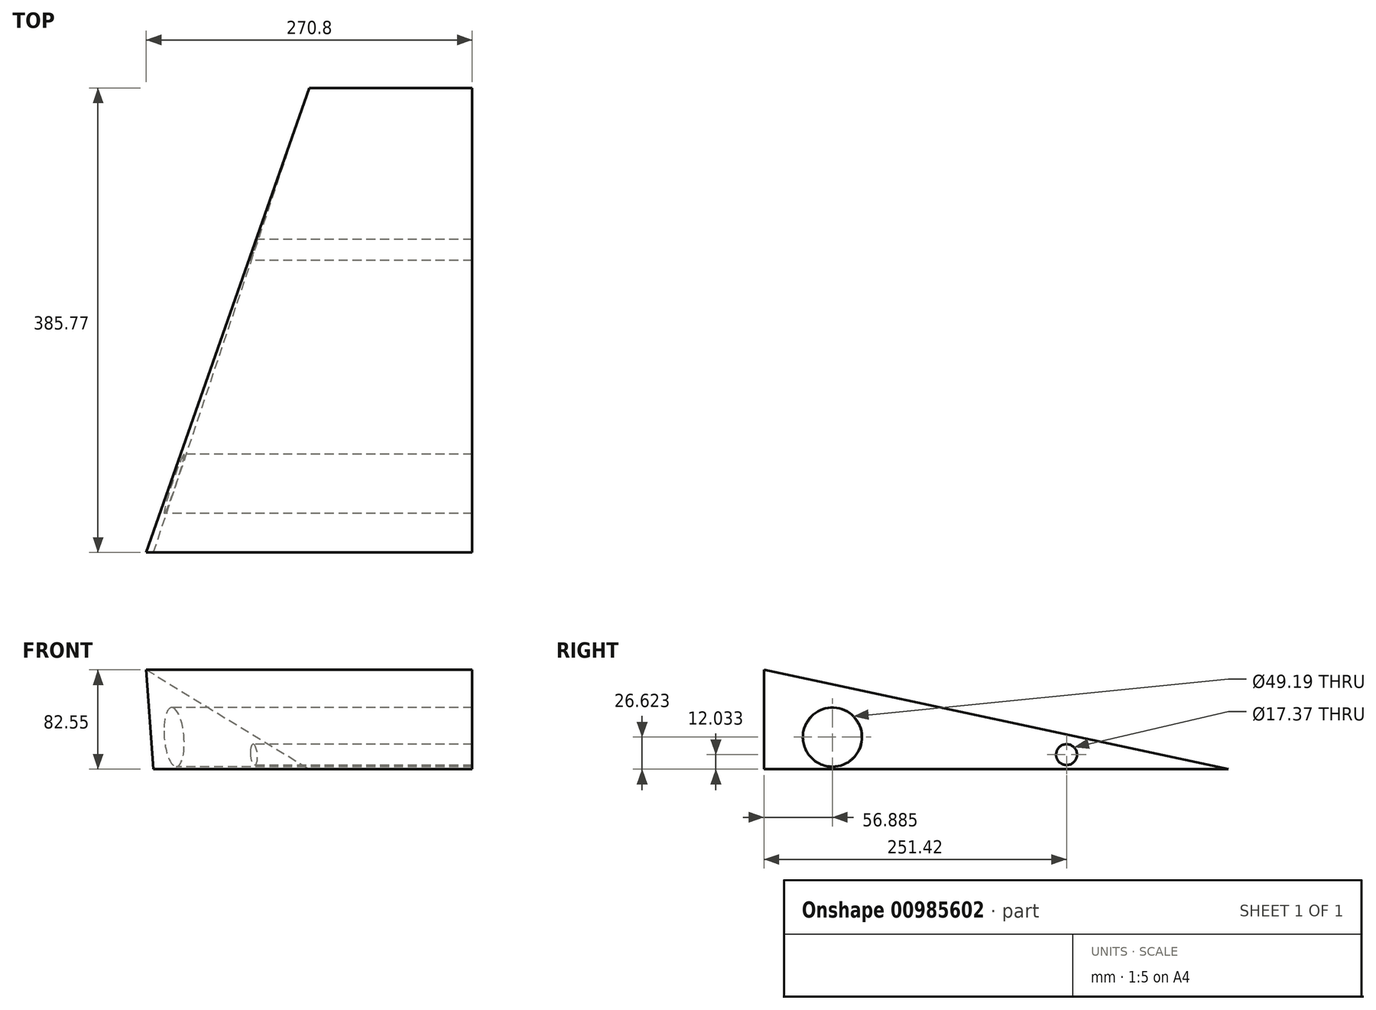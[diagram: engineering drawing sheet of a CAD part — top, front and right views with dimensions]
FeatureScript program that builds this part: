
annotation { "Feature Type Name" : "Feature", "Feature Type Description" : "" }
export const myFeature = defineFeature(function(context is Context, id is Id, definition is map)
    precondition{}
    {
        {
            var Q0;
            Q0=qCreatedBy(makeId("Top.planeOp"),FACE);
            var sketch = newSketch(context, id + "F0", { "sketchPlane" : qUnion([Q0])});
            skLineSegment(sketch, "E0.bottom", {"start": v(-122.77, 217) * mm, "end": v(148.03, 217) * mm});
            skLineSegment(sketch, "E0.top", {"start": v(-122.77, -168.76) * mm, "end": v(148.03, -168.76) * mm});
            skLineSegment(sketch, "E0.left", {"start": v(-122.77, 217) * mm, "end": v(-122.77, -168.76) * mm});
            skLineSegment(sketch, "E0.right", {"start": v(148.03, 217) * mm, "end": v(148.03, -168.76) * mm});
            skSolve(sketch);
        }
        {
            var Q0;
            Q0 = qSketchRegion(id + "F0", true);
            extrude(context, id + "F1", {"entities" : qUnion([Q0]), "depth" : 82.55 * mm, "offsetDistance" : 25.4 * mm});
        }
        {
            var Q0;
            Q0=makeQuery(id+"F1.opExtrude","SWEPT_FACE",FACE,{"disambiguationData":[OSD([sQuery(id+"F0.wireOp",EDGE,"E0.right")])]});
            var sketch = newSketch(context, id + "F2", { "sketchPlane" : qUnion([Q0])});
            skLineSegment(sketch, "E1", {"start": v(-168.76, 82.55) * mm, "end": v(217, 0) * mm});
            skSolve(sketch);
        }
        {
            var Q0;
            Q0=makeQuery(id+"F2.imprint","IMPRINT",FACE,{"disambiguationData":[TD([[makeQuery(id+"F2.imprint","IMPRINT",EDGE,{"derivedFrom":sQuery(id+"F2.wireOp",EDGE,"E1")}),1.0]])]});
            extrude(context, id + "F3", {"entities" : qUnion([Q0]), "operationType" : NewBodyOperationType.REMOVE, "oppositeDirection" : true, "depth" : 508 * mm, "offsetDistance" : 25.4 * mm});
        }
        {
            var Q0;
            Q0=makeQuery(id+"F3.boolean.opBoolean","COPY",FACE,{"derivedFrom":makeQuery(id+"F3.opExtrude","SWEPT_FACE",FACE,{"disambiguationData":[OSD([sQuery(id+"F2.wireOp",EDGE,"E1")])]})});
            var sketch = newSketch(context, id + "F4", { "sketchPlane" : qUnion([Q0])});
            skLineSegment(sketch, "E2", {"start": v(12.63, 212.2) * mm, "end": v(148.03, -182.3) * mm});
            skLineSegment(sketch, "E3", {"start": v(148.03, -182.3) * mm, "end": v(12.63, 212.2) * mm});
            skLineSegment(sketch, "E4", {"start": v(-122.77, -182.3) * mm, "end": v(12.63, 212.2) * mm});
            skSolve(sketch);
        }
        {
            var Q0;
            Q0=makeQuery(id+"F1.opExtrude","SWEPT_FACE",FACE,{"disambiguationData":[OSD([sQuery(id+"F0.wireOp",EDGE,"E0.left")])]});
            var sketch = newSketch(context, id + "F5", { "sketchPlane" : qUnion([Q0])});
            skCircle(sketch, "E5", {"center": v(-14.23, 20.02) * mm, "radius": 17.16 * mm});
            skCircle(sketch, "E6", {"center": v(111.88, 26.62) * mm, "radius": 24.6 * mm});
            skCircle(sketch, "E7", {"center": v(-56.6, 15.85) * mm, "radius": 9.54 * mm});
            skCircle(sketch, "E8", {"center": v(-82.66, 12.03) * mm, "radius": 8.68 * mm});
            skSolve(sketch);
        }
        {
            var Q0;
            Q0=makeQuery(id+"F5.imprint","IMPRINT",FACE,{"disambiguationData":[TD([[makeQuery(id+"F5.imprint","IMPRINT",EDGE,{"derivedFrom":sQuery(id+"F5.wireOp",EDGE,"E8")}),1.0]])]});
            var Q1;
            Q1=makeQuery(id+"F5.imprint","IMPRINT",FACE,{"disambiguationData":[TD([[makeQuery(id+"F5.imprint","IMPRINT",EDGE,{"derivedFrom":sQuery(id+"F5.wireOp",EDGE,"E6")}),1.0]])]});
            extrude(context, id + "F6", {"entities" : qUnion([Q0, Q1]), "operationType" : NewBodyOperationType.REMOVE, "oppositeDirection" : true, "depth" : 381 * mm, "offsetDistance" : 25.4 * mm});
        }
        {
            var Q0;
            {var subQ0=sQuery(id+"F4.wireOp",EDGE,"E3");Q0=makeQuery(id+"F4.imprint","IMPRINT",FACE,{"disambiguationData":[TD([[makeQuery(id+"F4.imprint","IMPRINT",EDGE,{"derivedFrom":subQ0}),-1.0]])]});}
            var Q1;
            {var subQ0=sQuery(id+"F4.wireOp",EDGE,"E4");Q1=makeQuery(id+"F4.imprint","IMPRINT",FACE,{"disambiguationData":[TD([[makeQuery(id+"F4.imprint","IMPRINT",EDGE,{"derivedFrom":subQ0}),1.0]])]});}
            extrude(context, id + "F7", {"entities" : qUnion([Q0, Q1]), "operationType" : NewBodyOperationType.REMOVE, "oppositeDirection" : true, "depth" : 1016 * mm, "offsetDistance" : 25.4 * mm});
        }
    });
